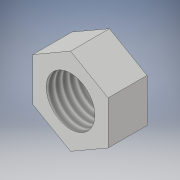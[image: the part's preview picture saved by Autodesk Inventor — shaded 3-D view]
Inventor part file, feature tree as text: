
AUTODESK INVENTOR PART (.ipt)
format: ipt  version: 2017 (Build 210142000, 142)  size: 102,912 bytes
history: native  units: in
note: dims shown in document units (in); Inventor stores cm internally (conversion verified against a paired STEP export)
features: extrude x1, thread x1, sketch x1
ambient origin geometry x8: Origin, YZ Plane, XZ Plane, XY Plane, X Axis, Y Axis, Z Axis, Center Point
bodies: Solid1 (feature_tree)
feature tree (3):
  extrude  "Extrusion1"  Depth=0.5in TaperAngle=0.0deg
  thread  "Thread1"  [1 undecoded]
  sketch  "Sketch1"  dims[d0=0.625in d1=0.5in d2=0.0in d3=1.0in d4=0.0in]
note: 1 required parameter value undecoded (feature->parameter linkage not recoverable at this tier; creation-order binding heuristic only, values carry confidence <= 0.55)
